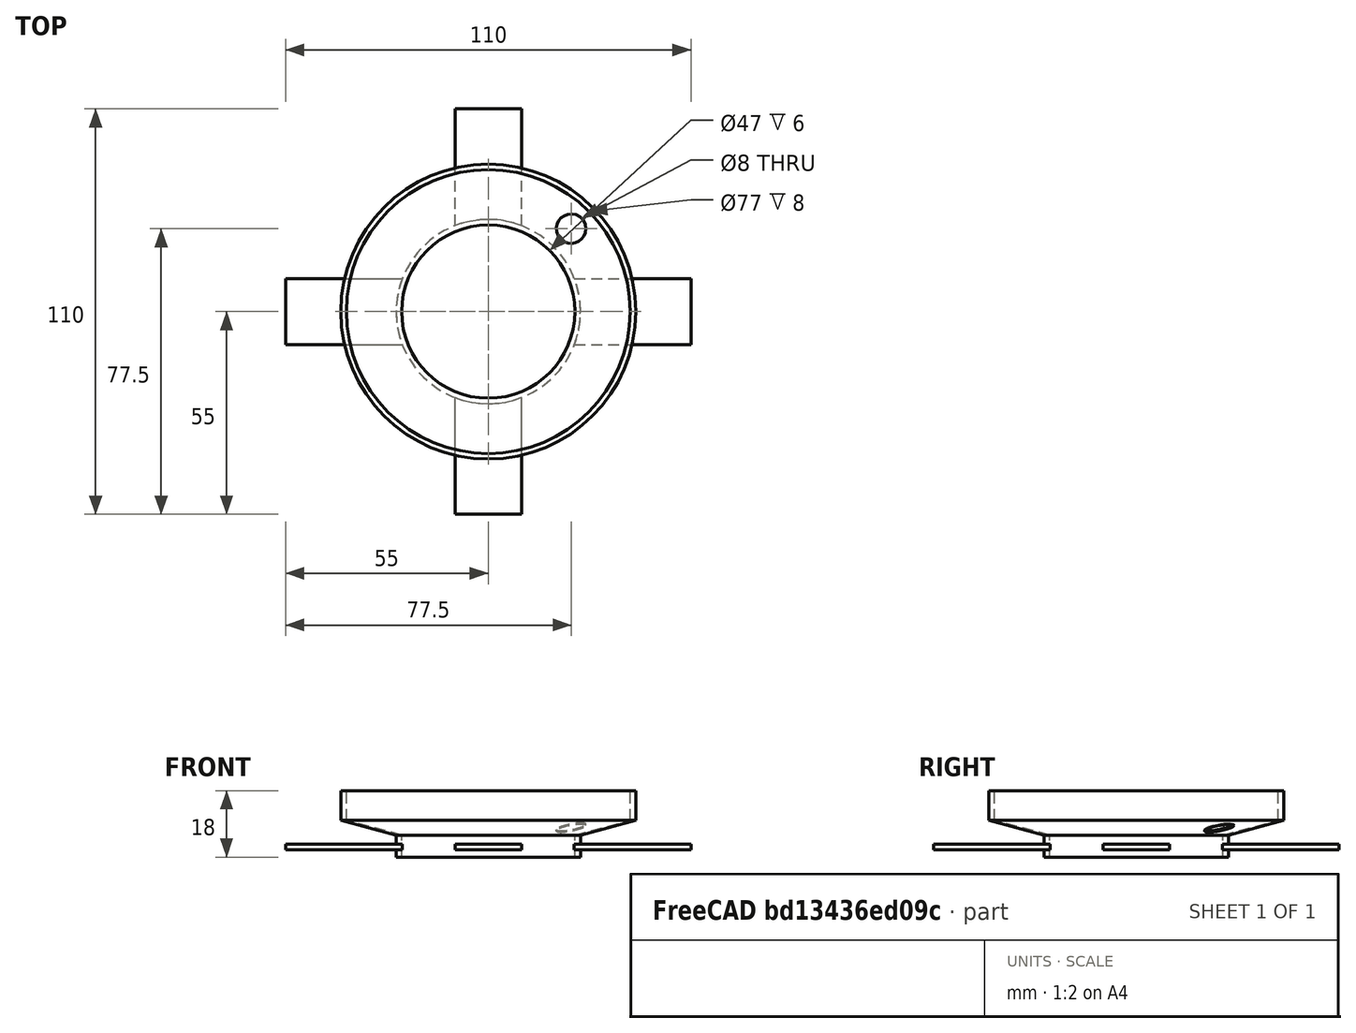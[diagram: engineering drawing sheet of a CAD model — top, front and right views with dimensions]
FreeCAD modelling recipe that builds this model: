
FCSTD DOCUMENT  (FreeCAD 0.15R4671 (Git))
Label: u-px-gnd-illuminator-base
License: All rights reserved
LicenseURL: http://es.wikipedia.org/wiki/Todos_los_derechos_reservados
objects: Part::Cylinder×6, Part::Cut×5, Part::Cone×2, Part::Box×2, Part::MultiFuse×2
note: 17 computed .brp shape members not serialized (recipe doc carries the construction recipe); baked Part::Feature solids carry a one-line shape summary decoded from their .brp

FEATURE [Part::Cone] Cone  label="Cono"
  Angle = 360
  Height = 4
  Placement = pos=(0,0,-12) rot=(0,0,1;0rad)
  Radius1 = 25
  Radius2 = 40
FEATURE [Part::Cylinder] Cylinder001  label="Cilindro001"
  Angle = 360
  Height = 8
  Placement = pos=(0,0,-8) rot=(0,0,1;0rad)
  Radius = 40
FEATURE [Part::Cylinder] Cylinder002  label="Cilindro002"
  Angle = 360
  Height = 8
  Placement = pos=(0,0,-8) rot=(0,0,1;0rad)
  Radius = 38.5
FEATURE [Part::Cut] Cut
  Base = -> Cylinder001
  Tool = -> Cylinder002
FEATURE [Part::Cone] Cone001  label="Cono001"
  Angle = 360
  Height = 4
  Placement = pos=(0,0,-12) rot=(0,0,1;0rad)
  Radius1 = 23.5
  Radius2 = 38.5
FEATURE [Part::Cut] Cut001
  Base = -> Cone
  Tool = -> Cone001
FEATURE [Part::Cylinder] Cylinder003  label="Cilindro003"
  Angle = 360
  Height = 6
  Placement = pos=(0,0,-18) rot=(0,0,1;0rad)
  Radius = 25
FEATURE [Part::Cylinder] Cylinder004  label="Cilindro004"
  Angle = 360
  Height = 6
  Placement = pos=(0,0,-18) rot=(0,0,1;0rad)
  Radius = 23.5
FEATURE [Part::Cut] Cut002
  Base = -> Cylinder003
  Tool = -> Cylinder004
FEATURE [Part::Box] Box  label="Cubo"
  Height = 1.5
  Length = 110
  Placement = pos=(-55,-9,0) rot=(0,0,1;0rad)
  Width = 18
FEATURE [Part::Box] Box001  label="Cubo001"
  Height = 1.5
  Length = 18
  Placement = pos=(-9,-55,0) rot=(0,0,1;0rad)
  Width = 110
FEATURE [Part::Cylinder] Cylinder005  label="Cilindro005"
  Angle = 360
  Height = 6
  Placement = pos=(0,0,-18) rot=(0,0,1;0rad)
  Radius = 25
FEATURE [Part::Cylinder] Cylinder  label="Cilindro"
  Angle = 360
  Height = 10
  Placement = pos=(22.5,22.5,-14) rot=(0,0,1;0rad)
  Radius = 4
FEATURE [Part::Cut] Cut004
  Base = -> Cut001
  Tool = -> Cylinder
FEATURE [Part::MultiFuse] Fusion
  Placement = pos=(0,0,-16) rot=(0,0,1;0rad)
  Shapes = -> [Box001,Box]
FEATURE [Part::Cut] Cut005
  Base = -> Fusion
  Tool = -> Cylinder005
FEATURE [Part::MultiFuse] Fusion001
  Shapes = -> [Cut,Cut002,Cut004,Cut005]
